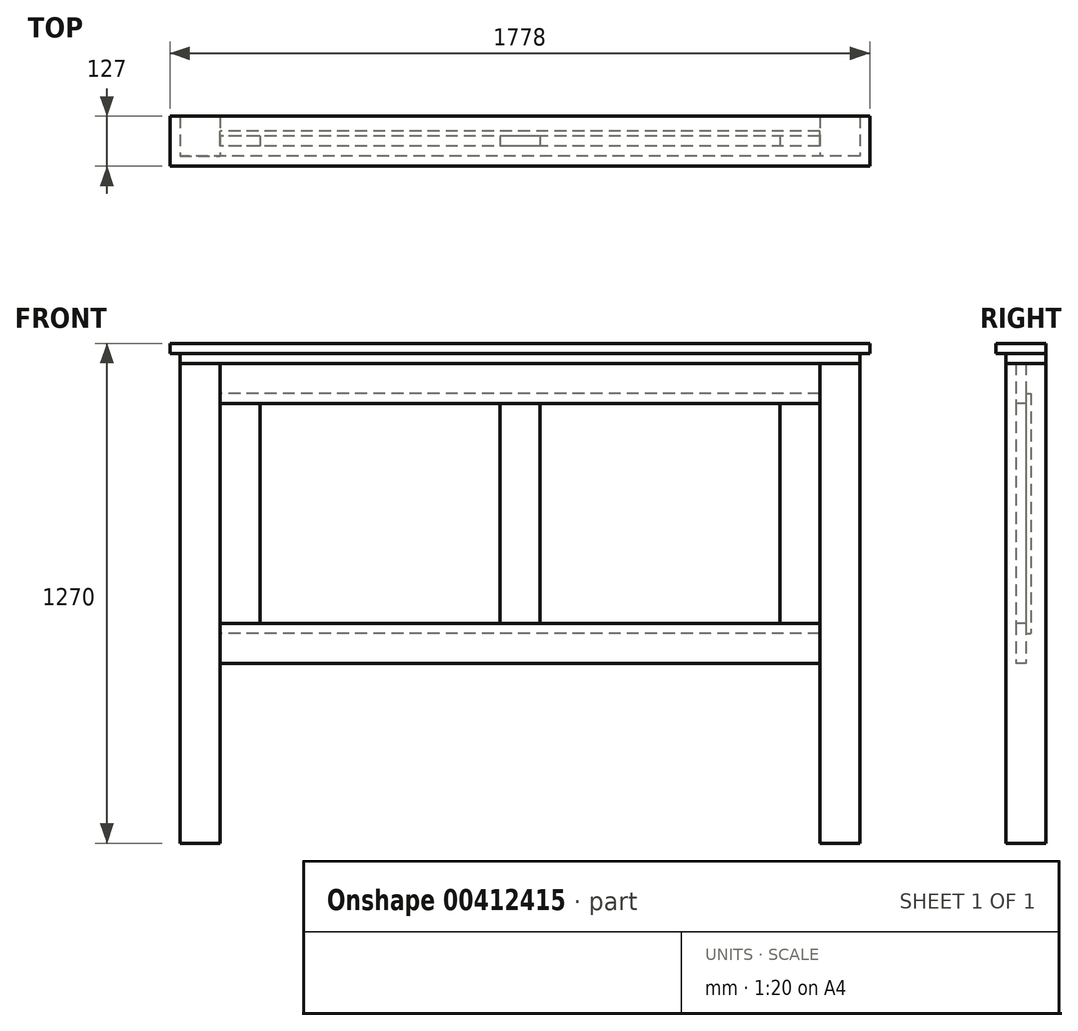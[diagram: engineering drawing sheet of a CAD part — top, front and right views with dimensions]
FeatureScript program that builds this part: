
annotation { "Feature Type Name" : "Feature", "Feature Type Description" : "" }
export const myFeature = defineFeature(function(context is Context, id is Id, definition is map)
    precondition{}
    {
        {
            var Q0;
            Q0=qCreatedBy(makeId("Top.planeOp"),FACE);
            var sketch = newSketch(context, id + "F0", { "sketchPlane" : qUnion([Q0])});
            skLineSegment(sketch, "E0.bottom", {"start": v(-863.6, 50.8) * mm, "end": v(-762, 50.8) * mm});
            skLineSegment(sketch, "E0.top", {"start": v(-863.6, -50.8) * mm, "end": v(-762, -50.8) * mm});
            skLineSegment(sketch, "E0.left", {"start": v(-863.6, 50.8) * mm, "end": v(-863.6, -50.8) * mm});
            skLineSegment(sketch, "E0.right", {"start": v(-762, 50.8) * mm, "end": v(-762, -50.8) * mm});
            skLineSegment(sketch, "E1", {"start": v(-1279.7, 0) * mm, "end": v(1080.44, 0) * mm, "construction": true});
            skPoint(sketch, "E1.endSnap0", {"position": v(-762, 0) * mm});
            skLineSegment(sketch, "E2", {"start": v(0, 373.74) * mm, "end": v(0, -1281.14) * mm, "construction": true});
            skSolve(sketch);
        }
        {
            var Q0;
            Q0 = qSketchRegion(id + "F0", true);
            extrude(context, id + "F1", {"entities" : qUnion([Q0]), "depth" : 1219.2 * mm});
        }
        {
            var Q0;
            Q0=makeQuery(id+"F1.opExtrude","SWEPT_BODY",BODY,{"disambiguationData":[OSD([sQuery(id+"F0.wireOp",EDGE,"E0.bottom"),sQuery(id+"F0.wireOp",EDGE,"E0.top"),sQuery(id+"F0.wireOp",EDGE,"E0.left"),sQuery(id+"F0.wireOp",EDGE,"E0.right")])]});
            var Q1;
            Q1=qCreatedBy(makeId("Right.planeOp"),FACE);
            mirror(context, id + "F2", {"entities" : qUnion([Q0]), "mirrorPlane" : qUnion([Q1])});
        }
        {
            var Q0;
            Q0=qCreatedBy(makeId("Right.planeOp"),FACE);
            var sketch = newSketch(context, id + "F3", { "sketchPlane" : qUnion([Q0])});
            skLineSegment(sketch, "E3", {"start": v(0, -29.82) * mm, "end": v(0, 398.56) * mm, "construction": true});
            skLineSegment(sketch, "E4.bottom", {"start": v(-25.4, 1219.2) * mm, "end": v(0, 1219.2) * mm});
            skLineSegment(sketch, "E4.top", {"start": v(-25.4, 1117.6) * mm, "end": v(0, 1117.6) * mm});
            skLineSegment(sketch, "E4.left", {"start": v(-25.4, 1219.2) * mm, "end": v(-25.4, 1117.6) * mm});
            skLineSegment(sketch, "E4.right", {"start": v(0, 1219.2) * mm, "end": v(0, 1117.6) * mm});
            skSolve(sketch);
        }
        {
            var Q0;
            Q0 = qSketchRegion(id + "F3", true);
            extrude(context, id + "F4", {"entities" : qUnion([Q0]), "endBound" : BoundingType.SYMMETRIC, "depth" : 1524 * mm});
        }
        {
            var Q0;
            Q0=qCreatedBy(makeId("Right.planeOp"),FACE);
            var sketch = newSketch(context, id + "F5", { "sketchPlane" : qUnion([Q0])});
            skLineSegment(sketch, "E5", {"start": v(0, -88.05) * mm, "end": v(0, 1881.86) * mm, "construction": true});
            skLineSegment(sketch, "E6.bottom", {"start": v(0, 558.8) * mm, "end": v(-25.4, 558.8) * mm});
            skLineSegment(sketch, "E6.top", {"start": v(0, 457.2) * mm, "end": v(-25.4, 457.2) * mm});
            skLineSegment(sketch, "E6.left", {"start": v(0, 558.8) * mm, "end": v(0, 457.2) * mm});
            skLineSegment(sketch, "E6.right", {"start": v(-25.4, 558.8) * mm, "end": v(-25.4, 457.2) * mm});
            skSolve(sketch);
        }
        {
            var Q0;
            Q0=makeQuery(id+"F5.imprint","IMPRINT",FACE,{"disambiguationData":[TD([[makeQuery(id+"F5.imprint","IMPRINT",EDGE,{"derivedFrom":sQuery(id+"F5.wireOp",EDGE,"E6.bottom")}),1.0]])]});
            extrude(context, id + "F6", {"entities" : qUnion([Q0]), "endBound" : BoundingType.SYMMETRIC, "depth" : 1524 * mm});
        }
        {
            var Q0;
            Q0=qCreatedBy(makeId("Right.planeOp"),FACE);
            var sketch = newSketch(context, id + "F7", { "sketchPlane" : qUnion([Q0])});
            skLineSegment(sketch, "E7", {"start": v(0, -58.2) * mm, "end": v(0, 1242.26) * mm, "construction": true});
            skLineSegment(sketch, "E8.bottom", {"start": v(0, 1143) * mm, "end": v(12.7, 1143) * mm});
            skLineSegment(sketch, "E8.top", {"start": v(0, 533.4) * mm, "end": v(12.7, 533.4) * mm});
            skLineSegment(sketch, "E8.left", {"start": v(0, 1143) * mm, "end": v(0, 533.4) * mm});
            skLineSegment(sketch, "E8.right", {"start": v(12.7, 1143) * mm, "end": v(12.7, 533.4) * mm});
            skSolve(sketch);
        }
        {
            var Q0;
            Q0 = qSketchRegion(id + "F7", true);
            extrude(context, id + "F8", {"entities" : qUnion([Q0]), "endBound" : BoundingType.SYMMETRIC, "depth" : 1524 * mm});
        }
        {
            var Q0;
            Q0=makeQuery(id+"F6.opExtrude","SWEPT_FACE",FACE,{"disambiguationData":[OSD([sQuery(id+"F5.wireOp",EDGE,"E6.bottom")])]});
            var sketch = newSketch(context, id + "F9", { "sketchPlane" : qUnion([Q0])});
            skLineSegment(sketch, "E9.bottom", {"start": v(-762, 0) * mm, "end": v(-660.4, 0) * mm});
            skLineSegment(sketch, "E9.top", {"start": v(-762, -25.4) * mm, "end": v(-660.4, -25.4) * mm});
            skLineSegment(sketch, "E9.left", {"start": v(-762, 0) * mm, "end": v(-762, -25.4) * mm});
            skLineSegment(sketch, "E9.right", {"start": v(-660.4, 0) * mm, "end": v(-660.4, -25.4) * mm});
            skLineSegment(sketch, "E10.bottom", {"start": v(762, 0) * mm, "end": v(660.4, 0) * mm});
            skLineSegment(sketch, "E10.top", {"start": v(762, -25.4) * mm, "end": v(660.4, -25.4) * mm});
            skLineSegment(sketch, "E10.left", {"start": v(762, 0) * mm, "end": v(762, -25.4) * mm});
            skLineSegment(sketch, "E10.right", {"start": v(660.4, 0) * mm, "end": v(660.4, -25.4) * mm});
            skLineSegment(sketch, "E11.bottom", {"start": v(-50.8, 0) * mm, "end": v(50.8, 0) * mm});
            skLineSegment(sketch, "E11.top", {"start": v(-50.8, -25.4) * mm, "end": v(50.8, -25.4) * mm});
            skLineSegment(sketch, "E11.left", {"start": v(-50.8, 0) * mm, "end": v(-50.8, -25.4) * mm});
            skLineSegment(sketch, "E11.right", {"start": v(50.8, 0) * mm, "end": v(50.8, -25.4) * mm});
            skLineSegment(sketch, "E12", {"start": v(0, 0) * mm, "end": v(0, -103.95) * mm, "construction": true});
            skSolve(sketch);
        }
        {
            var Q0;
            Q0 = qSketchRegion(id + "F9", true);
            extrude(context, id + "F10", {"entities" : qUnion([Q0]), "depth" : 558.8 * mm});
        }
        {
            var Q0;
            Q0=qCreatedBy(makeId("Right.planeOp"),FACE);
            var sketch = newSketch(context, id + "F11", { "sketchPlane" : qUnion([Q0])});
            skLineSegment(sketch, "E13.bottom", {"start": v(-50.8, 1219.2) * mm, "end": v(50.8, 1219.2) * mm});
            skLineSegment(sketch, "E13.top", {"start": v(-50.8, 1244.6) * mm, "end": v(50.8, 1244.6) * mm});
            skLineSegment(sketch, "E13.left", {"start": v(-50.8, 1219.2) * mm, "end": v(-50.8, 1244.6) * mm});
            skLineSegment(sketch, "E13.right", {"start": v(50.8, 1219.2) * mm, "end": v(50.8, 1244.6) * mm});
            skSolve(sketch);
        }
        {
            var Q0;
            Q0 = qSketchRegion(id + "F11", true);
            extrude(context, id + "F12", {"entities" : qUnion([Q0]), "endBound" : BoundingType.SYMMETRIC, "depth" : 1727.2 * mm});
        }
        {
            var Q0;
            Q0=qCreatedBy(makeId("Right.planeOp"),FACE);
            var sketch = newSketch(context, id + "F13", { "sketchPlane" : qUnion([Q0])});
            skLineSegment(sketch, "E14", {"start": v(0, 1318.12) * mm, "end": v(0, 1099.8) * mm, "construction": true});
            skLineSegment(sketch, "E15.bottom", {"start": v(-76.2, 1270) * mm, "end": v(50.8, 1270) * mm});
            skLineSegment(sketch, "E15.top", {"start": v(-76.2, 1244.6) * mm, "end": v(50.8, 1244.6) * mm});
            skLineSegment(sketch, "E15.left", {"start": v(-76.2, 1270) * mm, "end": v(-76.2, 1244.6) * mm});
            skLineSegment(sketch, "E15.right", {"start": v(50.8, 1270) * mm, "end": v(50.8, 1244.6) * mm});
            skSolve(sketch);
        }
        {
            var Q0;
            Q0 = qSketchRegion(id + "F13", true);
            extrude(context, id + "F14", {"entities" : qUnion([Q0]), "operationType" : NewBodyOperationType.ADD, "endBound" : BoundingType.SYMMETRIC, "depth" : 1778 * mm});
        }
    });
